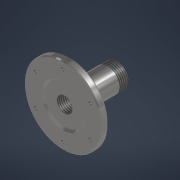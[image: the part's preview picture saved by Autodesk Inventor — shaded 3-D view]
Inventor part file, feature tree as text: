
AUTODESK INVENTOR PART (.ipt)
format: ipt  version: 2022 (Build 260153000, 153)  size: 203,264 bytes
history: native  units: mm
features: chamfer x6, thread x2, sketch x2, reference x2, other x2, revolve x1, hole x1, fillet x1
ambient origin geometry x8: Origin, YZ Plane, XZ Plane, XY Plane, X Axis, Y Axis, Z Axis, Center Point
bodies: Solid1 (feature_tree)
feature tree (17):
  revolve  "Revolution1"  [1 undecoded]
  chamfer  "Chamfer1"  Distance=25.0mm
  chamfer  "Chamfer2"  Distance=36.0mm
  hole  "Hole1"  [1 undecoded]
  chamfer  "Chamfer3"  Angle=360.0deg  [1 undecoded]
  chamfer  "Chamfer5"  Distance=8.0mm
  thread  "Thread2"  [1 undecoded]
  chamfer  "Chamfer6"  Distance=8.0mm Angle=30.0deg
  thread  "Thread3"  [1 undecoded]
  chamfer  "Chamfer7"  Distance=65.0mm
  fillet  "Fillet1"  Radius=60.0mm
  sketch  "Sketch1"  dims[d1=80.0mm d2=2.0mm]
  reference  "Reference1"
  reference  "Reference2"
  sketch  "Sketch2"  dims[d3=8.0mm d4=25.0mm d5=36.0mm d11=16.0mm d13=360.0deg d16=8.0mm d17=38.0mm d18=8.0mm d19=2.0mm d20=30.0deg d21=2.0mm d22=2.0mm d23=45.0deg d24=65.0mm d25=60.0mm d27=360.0deg d29=3.242mm d30=8.0mm d31=6.5mm d32=3.4mm d33=90.0deg d34=11.8mm d35=20.594885mm d41=1.0mm d42=2.0mm d43=45.0deg d47=1.0mm d48=2.0mm d49=45.0deg d50=1.0mm d52=14.0mm d53=0.0mm d54=2.0mm d55=2.0mm d56=45.0deg d57=34.0mm d58=10.0mm d59=0.0mm d60=1.0mm d61=2.0mm d62=45.0deg d63=2.0mm d64=40.0mm d65=0.5mm]
  other  "SistemaElevacionV2.iam"
  other  "Soporte:1"
note: 5 required parameter values undecoded (feature->parameter linkage not recoverable at this tier; creation-order binding heuristic only, values carry confidence <= 0.55)